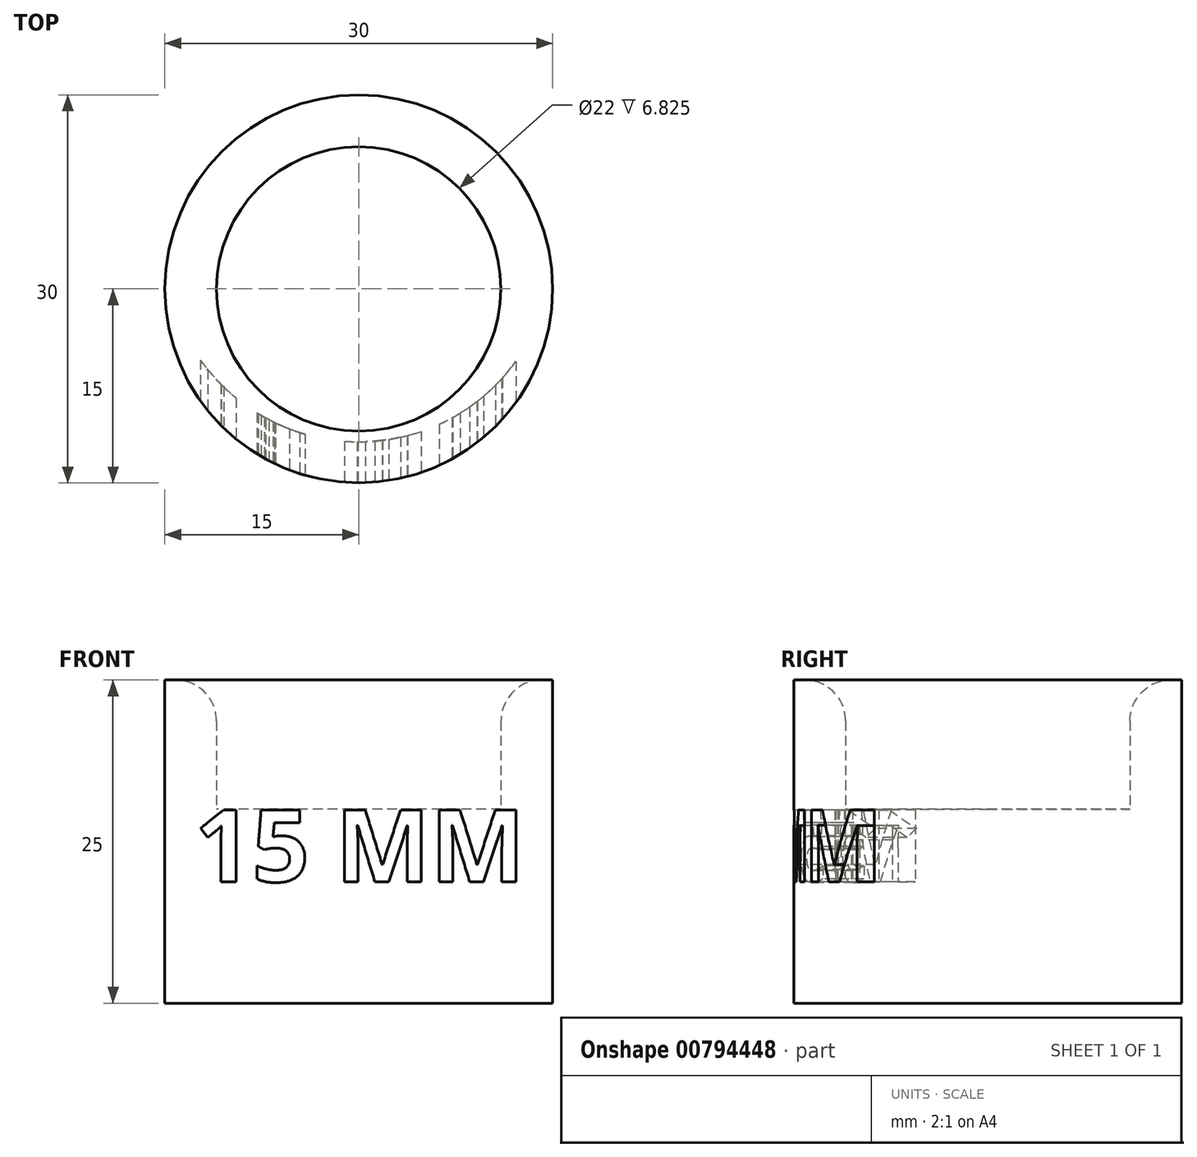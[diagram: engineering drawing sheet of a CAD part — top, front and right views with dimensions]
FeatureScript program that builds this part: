
annotation { "Feature Type Name" : "Feature", "Feature Type Description" : "" }
export const myFeature = defineFeature(function(context is Context, id is Id, definition is map)
    precondition{}
    {
        {
            var Q0;
            Q0=qCreatedBy(makeId("Top.planeOp"),FACE);
            var sketch = newSketch(context, id + "F0", { "sketchPlane" : qUnion([Q0])});
            skCircle(sketch, "E0", {"center": v(0, 0) * mm, "radius": 11 * mm});
            skCircle(sketch, "E1", {"center": v(0, 0) * mm, "radius": 15 * mm});
            skSolve(sketch);
        }
        {
            var Q0;
            Q0=makeQuery(id+"F0.imprint","IMPRINT",FACE,{"disambiguationData":[TD([[makeQuery(id+"F0.imprint","IMPRINT",EDGE,{"derivedFrom":sQuery(id+"F0.wireOp",EDGE,"E0")}),-1.0]])]});
            extrude(context, id + "F1", {"entities" : qUnion([Q0]), "depth" : 10 * mm, "offsetDistance" : 25.4 * mm});
        }
        {
            var Q0;
            Q0=makeQuery(id+"F1.opExtrude","CAP_EDGE",EDGE,{"disambiguationData":[OSD([sQuery(id+"F0.wireOp",EDGE,"E0")])],"isStart":false});
            fillet(context, id + "F2", {"entities" : qUnion([Q0]), "radius" : 3.17 * mm, "tangentPropagation" : true, "allowEdgeOverflow" : false});
        }
        {
            var Q0;
            Q0=makeQuery(id+"F1.opExtrude","CAP_FACE",FACE,{"disambiguationData":[OSD([sQuery(id+"F0.wireOp",EDGE,"E0"),sQuery(id+"F0.wireOp",EDGE,"E1")])],"isStart":true});
            var sketch = newSketch(context, id + "F3", { "sketchPlane" : qUnion([Q0])});
            skCircle(sketch, "E2.0", {"center": v(0, 0) * mm, "radius": 15 * mm});
            skSolve(sketch);
        }
        {
            var Q0;
            Q0=makeQuery(id+"F3.imprint","IMPRINT",FACE,{"disambiguationData":[TD([[makeQuery(id+"F3.imprint","IMPRINT",EDGE,{"derivedFrom":makeQuery(id+"F1.opExtrude","CAP_EDGE",EDGE,{"disambiguationData":[OSD([sQuery(id+"F0.wireOp",EDGE,"E0")])],"isStart":true})}),-1.0]])]});
            var Q1;
            Q1=makeQuery(id+"F3.imprint","IMPRINT",FACE,{"disambiguationData":[TD([[makeQuery(id+"F3.imprint","IMPRINT",EDGE,{"derivedFrom":sQuery(id+"F3.wireOp",EDGE,"E2.0")}),-1.0]])]});
            extrude(context, id + "F4", {"entities" : qUnion([Q0, Q1]), "operationType" : NewBodyOperationType.ADD, "depth" : 15 * mm, "offsetDistance" : 25.4 * mm});
        }
        {
            var Q0;
            Q0=qCreatedBy(makeId("Front.planeOp"),FACE);
            cPlane(context, id + "F5", {"entities" : qUnion([Q0]), "cplaneType" : CPlaneType.OFFSET, "offset" : 15 * mm, "width" : 152.4 * mm, "height" : 152.4 * mm});
        }
        {
            var Q0;
            Q0=qCreatedBy(id+"F5.planeOp",FACE);
            var sketch = newSketch(context, id + "F6", { "sketchPlane" : qUnion([Q0])});
            skText(sketch, "E3", { "text": "15 MM", "fontName": "OpenSans-Bold.ttf"});
            const initialGuessF6  = {"E3": [-0.0127, -0.0056, 1, 0, 0.0056]};
            skSetInitialGuess(sketch, initialGuessF6);
            skSolve(sketch);
        }
        {
            var Q0;
            Q0=makeQuery(id+"F6.imprint","IMPRINT",FACE,{"disambiguationData":[TD([[makeQuery(id+"F6.imprint","IMPRINT",EDGE,{"derivedFrom":sQuery(id+"F6.wireOp",EDGE,"E3.sketch_text.stroke-0")}),-1.0]])]});
            var Q1;
            Q1=makeQuery(id+"F6.imprint","IMPRINT",FACE,{"disambiguationData":[TD([[makeQuery(id+"F6.imprint","IMPRINT",EDGE,{"derivedFrom":sQuery(id+"F6.wireOp",EDGE,"E3.sketch_text.stroke-10")}),-1.0]])]});
            var Q2;
            Q2=makeQuery(id+"F6.imprint","IMPRINT",FACE,{"disambiguationData":[TD([[makeQuery(id+"F6.imprint","IMPRINT",EDGE,{"derivedFrom":sQuery(id+"F6.wireOp",EDGE,"E3.sketch_text.stroke-30")}),-1.0]])]});
            var Q3;
            Q3=makeQuery(id+"F6.imprint","IMPRINT",FACE,{"disambiguationData":[TD([[makeQuery(id+"F6.imprint","IMPRINT",EDGE,{"derivedFrom":sQuery(id+"F6.wireOp",EDGE,"E3.sketch_text.stroke-49")}),-1.0]])]});
            var Q4;
            Q4=makeQuery(id+"F4.boolean.opBoolean","MERGE",FACE,{"derivedFrom":[makeQuery(id+"F1.opExtrude","SWEPT_FACE",FACE,{"disambiguationData":[OSD([sQuery(id+"F0.wireOp",EDGE,"E1")])]}),makeQuery(id+"F4.opExtrude","SWEPT_FACE",FACE,{"disambiguationData":[OSD([sQuery(id+"F3.wireOp",EDGE,"E2.0")])]})]});
            extrude(context, id + "F7", {"entities" : qUnion([Q0, Q1, Q2, Q3]), "operationType" : NewBodyOperationType.REMOVE, "endBound" : BoundingType.UP_TO_SURFACE, "oppositeDirection" : true, "depth" : 25.4 * mm, "endBoundEntityFace" : qUnion([Q4]), "hasOffset" : true, "offsetDistance" : -3.17 * mm});
        }
    });
